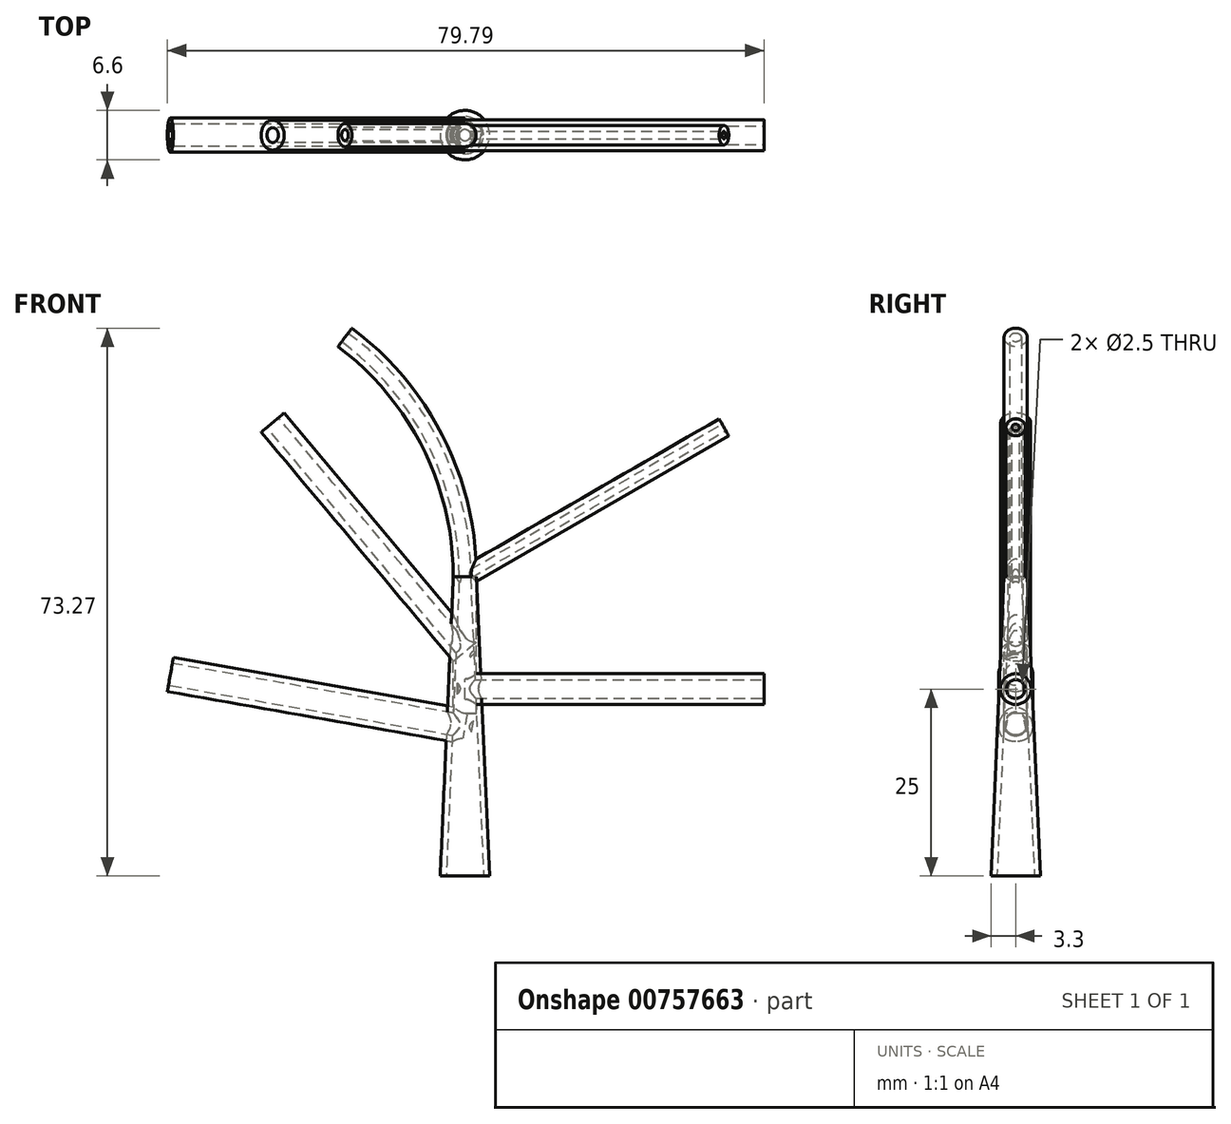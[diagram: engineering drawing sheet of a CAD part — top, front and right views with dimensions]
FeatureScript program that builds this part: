
annotation { "Feature Type Name" : "Feature", "Feature Type Description" : "" }
export const myFeature = defineFeature(function(context is Context, id is Id, definition is map)
    precondition{}
    {
        {
            var Q0;
            Q0=qCreatedBy(makeId("Top.planeOp"),FACE);
            var sketch = newSketch(context, id + "F0", { "sketchPlane" : qUnion([Q0])});
            skCircle(sketch, "E0", {"center": v(0, 0) * mm, "radius": 1.55 * mm});
            skSolve(sketch);
        }
        {
            var Q0;
            Q0=qCreatedBy(makeId("Front.planeOp"),FACE);
            var sketch = newSketch(context, id + "F1", { "sketchPlane" : qUnion([Q0])});
            skLineSegment(sketch, "E1", {"start": v(0, 0) * mm, "end": v(0, 40) * mm});
            skLineSegment(sketch, "E2", {"start": v(0, 40) * mm, "end": v(-40, 40) * mm, "construction": true});
            skArc(sketch, "E3", {"start": v(0, 40) * mm, "mid": v(-4.23, 57.9) * mm, "end": v(-16.04, 72.03) * mm});
            skSolve(sketch);
        }
        {
            var Q0;
            Q0 = qSketchRegion(id + "F0", true);
            var Q1;
            Q1 = qConstructionFilter(qBodyType(qCreatedBy(id + "F1" ,EDGE), BodyType.WIRE), ConstructionObject.NO);
            sweep(context, id + "F2", {"profiles" : qUnion([Q0]), "path" : qUnion([Q1])});
        }
        {
            var Q0;
            Q0=qCreatedBy(makeId("Right.planeOp"),FACE);
            var sketch = newSketch(context, id + "F3", { "sketchPlane" : qUnion([Q0])});
            skLineSegment(sketch, "E4", {"start": v(0, 40) * mm, "end": v(-37, 40) * mm});
            skSolve(sketch);
        }
        {
            var Q0;
            Q0=qCreatedBy(makeId("Right.planeOp"),FACE);
            var Q1;
            Q1=sQuery(id+"F3.wireOp",EDGE,"E4");
            cPlane(context, id + "F4", {"entities" : qUnion([Q0, Q1]), "cplaneType" : CPlaneType.LINE_ANGLE, "offset" : 25 * mm, "angle" : 30 * degree, "width" : 150 * mm, "height" : 150 * mm});
        }
        {
            var Q0;
            Q0=qCreatedBy(id+"F4.planeOp",FACE);
            var sketch = newSketch(context, id + "F5", { "sketchPlane" : qUnion([Q0])});
            skCircle(sketch, "E5", {"center": v(0, 34.64) * mm, "radius": 1.3 * mm});
            skSolve(sketch);
        }
        {
            var Q0;
            Q0 = qSketchRegion(id + "F5", true);
            extrude(context, id + "F6", {"entities" : qUnion([Q0]), "operationType" : NewBodyOperationType.ADD, "oppositeDirection" : true, "depth" : 40 * mm, "offsetDistance" : 25 * mm});
        }
        {
            var Q0;
            Q0=qCreatedBy(makeId("Right.planeOp"),FACE);
            var sketch = newSketch(context, id + "F7", { "sketchPlane" : qUnion([Q0])});
            skLineSegment(sketch, "E6", {"start": v(0, 0) * mm, "end": v(0, 30) * mm, "construction": true});
            skLineSegment(sketch, "E7", {"start": v(0, 30) * mm, "end": v(-66.79, 30) * mm});
            skSolve(sketch);
        }
        {
            var Q0;
            Q0=qCreatedBy(makeId("Right.planeOp"),FACE);
            var Q1;
            Q1=sQuery(id+"F7.wireOp",EDGE,"E7");
            cPlane(context, id + "F8", {"entities" : qUnion([Q0, Q1]), "cplaneType" : CPlaneType.LINE_ANGLE, "offset" : 25 * mm, "angle" : 130 * degree, "width" : 150 * mm, "height" : 150 * mm});
        }
        {
            var Q0;
            Q0=qCreatedBy(id+"F8.planeOp",FACE);
            var sketch = newSketch(context, id + "F9", { "sketchPlane" : qUnion([Q0])});
            skCircle(sketch, "E8", {"center": v(19.28, 0) * mm, "radius": 2 * mm});
            skSolve(sketch);
        }
        {
            var Q0;
            Q0 = qSketchRegion(id + "F9", true);
            extrude(context, id + "F10", {"entities" : qUnion([Q0]), "operationType" : NewBodyOperationType.ADD, "oppositeDirection" : true, "depth" : 40 * mm, "offsetDistance" : 25 * mm});
        }
        {
            var Q0;
            Q0=qCreatedBy(makeId("Right.planeOp"),FACE);
            var sketch = newSketch(context, id + "F11", { "sketchPlane" : qUnion([Q0])});
            skLineSegment(sketch, "E9", {"start": v(0, 20) * mm, "end": v(-34.38, 20) * mm});
            skSolve(sketch);
        }
        {
            var Q0;
            Q0=qCreatedBy(makeId("Right.planeOp"),FACE);
            var Q1;
            Q1=sQuery(id+"F11.wireOp",EDGE,"E9");
            cPlane(context, id + "F12", {"entities" : qUnion([Q0, Q1]), "cplaneType" : CPlaneType.LINE_ANGLE, "offset" : 25 * mm, "angle" : 170 * degree, "width" : 150 * mm, "height" : 150 * mm});
        }
        {
            var Q0;
            Q0=qCreatedBy(id+"F12.planeOp",FACE);
            var sketch = newSketch(context, id + "F13", { "sketchPlane" : qUnion([Q0])});
            skCircle(sketch, "E10", {"center": v(0, 19.7) * mm, "radius": 2.3 * mm});
            skSolve(sketch);
        }
        {
            var Q0;
            Q0 = qSketchRegion(id + "F13", true);
            extrude(context, id + "F14", {"entities" : qUnion([Q0]), "operationType" : NewBodyOperationType.ADD, "oppositeDirection" : true, "depth" : 40 * mm, "offsetDistance" : 25 * mm});
        }
        {
            var Q0;
            Q0=qCreatedBy(makeId("Right.planeOp"),FACE);
            var sketch = newSketch(context, id + "F15", { "sketchPlane" : qUnion([Q0])});
            skCircle(sketch, "E11", {"center": v(0, 25) * mm, "radius": 2.05 * mm});
            skSolve(sketch);
        }
        {
            var Q0;
            Q0 = qSketchRegion(id + "F15", true);
            extrude(context, id + "F16", {"entities" : qUnion([Q0]), "operationType" : NewBodyOperationType.ADD, "depth" : 40 * mm, "offsetDistance" : 25 * mm});
        }
        {
            var Q0;
            Q0=qCreatedBy(makeId("Front.planeOp"),FACE);
            var sketch = newSketch(context, id + "F17", { "sketchPlane" : qUnion([Q0])});
            skLineSegment(sketch, "E12", {"start": v(2.5, 0) * mm, "end": v(3.3, 0) * mm});
            skLineSegment(sketch, "E13", {"start": v(0.75, 40) * mm, "end": v(1.55, 40) * mm});
            skLineSegment(sketch, "E14", {"start": v(1.55, 40) * mm, "end": v(3.3, 0) * mm});
            skLineSegment(sketch, "E15", {"start": v(0.75, 40) * mm, "end": v(2.5, 0) * mm});
            skSolve(sketch);
        }
        {
            var Q0;
            Q0=qCreatedBy(makeId("Front.planeOp"),FACE);
            var sketch = newSketch(context, id + "F18", { "sketchPlane" : qUnion([Q0])});
            skLineSegment(sketch, "E16", {"start": v(0, 0) * mm, "end": v(0, 37.36) * mm});
            skSolve(sketch);
        }
        {
            var Q0;
            Q0 = qSketchRegion(id + "F17", true);
            var Q1;
            Q1=sQuery(id+"F18.wireOp",EDGE,"E16");
            revolve(context, id + "F19", {"surfaceOperationType" : NewSurfaceOperationType.NEW, "entities" : qUnion([Q0]), "axis" : qUnion([Q1]), "revolveType" : RevolveType.FULL});
        }
        {
            var Q0;
            Q0=qCreatedBy(makeId("Front.planeOp"),FACE);
            var sketch = newSketch(context, id + "F20", { "sketchPlane" : qUnion([Q0])});
            skLineSegment(sketch, "E17", {"start": v(0, 0) * mm, "end": v(0, 40) * mm});
            skLineSegment(sketch, "E18", {"start": v(0, 40) * mm, "end": v(0.75, 40) * mm});
            skLineSegment(sketch, "E19", {"start": v(0, 0) * mm, "end": v(2.5, 0) * mm});
            skLineSegment(sketch, "E20", {"start": v(2.5, 0) * mm, "end": v(0.75, 40) * mm});
            skSolve(sketch);
        }
        {
            var Q0;
            Q0 = qSketchRegion(id + "F20", true);
            var Q1;
            Q1=sQuery(id+"F20.wireOp",EDGE,"E17");
            revolve(context, id + "F21", {"operationType" : NewBodyOperationType.REMOVE, "surfaceOperationType" : NewSurfaceOperationType.NEW, "entities" : qUnion([Q0]), "axis" : qUnion([Q1]), "revolveType" : RevolveType.FULL, "oppositeDirection" : true});
        }
        {
            var Q0;
            Q0=makeQuery(id+"F14.opExtrude","CAP_FACE",FACE,{"disambiguationData":[OSD([sQuery(id+"F13.wireOp",EDGE,"E10")])],"isStart":false});
            var sketch = newSketch(context, id + "F22", { "sketchPlane" : qUnion([Q0])});
            skCircle(sketch, "E21", {"center": v(0, 19.7) * mm, "radius": 1.5 * mm});
            skSolve(sketch);
        }
        {
            var Q0;
            Q0 = qSketchRegion(id + "F22", true);
            extrude(context, id + "F23", {"entities" : qUnion([Q0]), "operationType" : NewBodyOperationType.REMOVE, "oppositeDirection" : true, "depth" : 41 * mm, "offsetDistance" : 25 * mm});
        }
        {
            var Q0;
            Q0=makeQuery(id+"F16.opExtrude","CAP_FACE",FACE,{"disambiguationData":[OSD([sQuery(id+"F15.wireOp",EDGE,"E11")])],"isStart":false});
            var sketch = newSketch(context, id + "F24", { "sketchPlane" : qUnion([Q0])});
            skCircle(sketch, "E22", {"center": v(0, 25) * mm, "radius": 1.25 * mm});
            skSolve(sketch);
        }
        {
            var Q0;
            Q0 = qSketchRegion(id + "F24", true);
            extrude(context, id + "F25", {"entities" : qUnion([Q0]), "operationType" : NewBodyOperationType.REMOVE, "oppositeDirection" : true, "depth" : 41 * mm, "offsetDistance" : 25 * mm});
        }
        {
            var Q0;
            Q0=makeQuery(id+"F10.opExtrude","CAP_FACE",FACE,{"disambiguationData":[OSD([sQuery(id+"F9.wireOp",EDGE,"E8")])],"isStart":false});
            var sketch = newSketch(context, id + "F26", { "sketchPlane" : qUnion([Q0])});
            skCircle(sketch, "E23", {"center": v(19.28, 0) * mm, "radius": 1 * mm});
            skSolve(sketch);
        }
        {
            var Q0;
            Q0 = qSketchRegion(id + "F26", true);
            extrude(context, id + "F27", {"entities" : qUnion([Q0]), "operationType" : NewBodyOperationType.REMOVE, "oppositeDirection" : true, "depth" : 41 * mm, "offsetDistance" : 25 * mm});
        }
        {
            var Q0;
            Q0=makeQuery(id+"F2.opSweep","CAP_FACE",FACE,{"disambiguationData":[OSD([sQuery(id+"F0.wireOp",EDGE,"E0"),sQuery(id+"F1.wireOp",VERTEX,"E3.end")])],"isStart":false});
            var sketch = newSketch(context, id + "F28", { "sketchPlane" : qUnion([Q0])});
            skCircle(sketch, "E24", {"center": v(0, 48.07) * mm, "radius": 0.75 * mm});
            skSolve(sketch);
        }
        {
            var Q0;
            Q0 = qSketchRegion(id + "F28", true);
            var Q1;
            Q1 = qConstructionFilter(qBodyType(qCreatedBy(id + "F1" ,EDGE), BodyType.WIRE), ConstructionObject.NO);
            sweep(context, id + "F29", {"operationType" : NewBodyOperationType.REMOVE, "profiles" : qUnion([Q0]), "path" : qUnion([Q1])});
        }
        {
            var Q0;
            Q0=makeQuery(id+"F6.opExtrude","CAP_FACE",FACE,{"disambiguationData":[OSD([sQuery(id+"F5.wireOp",EDGE,"E5")])],"isStart":false});
            var sketch = newSketch(context, id + "F30", { "sketchPlane" : qUnion([Q0])});
            skCircle(sketch, "E25", {"center": v(0, 34.64) * mm, "radius": 0.5 * mm});
            skSolve(sketch);
        }
        {
            var Q0;
            Q0 = qSketchRegion(id + "F30", true);
            extrude(context, id + "F31", {"entities" : qUnion([Q0]), "operationType" : NewBodyOperationType.REMOVE, "oppositeDirection" : true, "depth" : 41 * mm, "offsetDistance" : 25 * mm});
        }
    });
